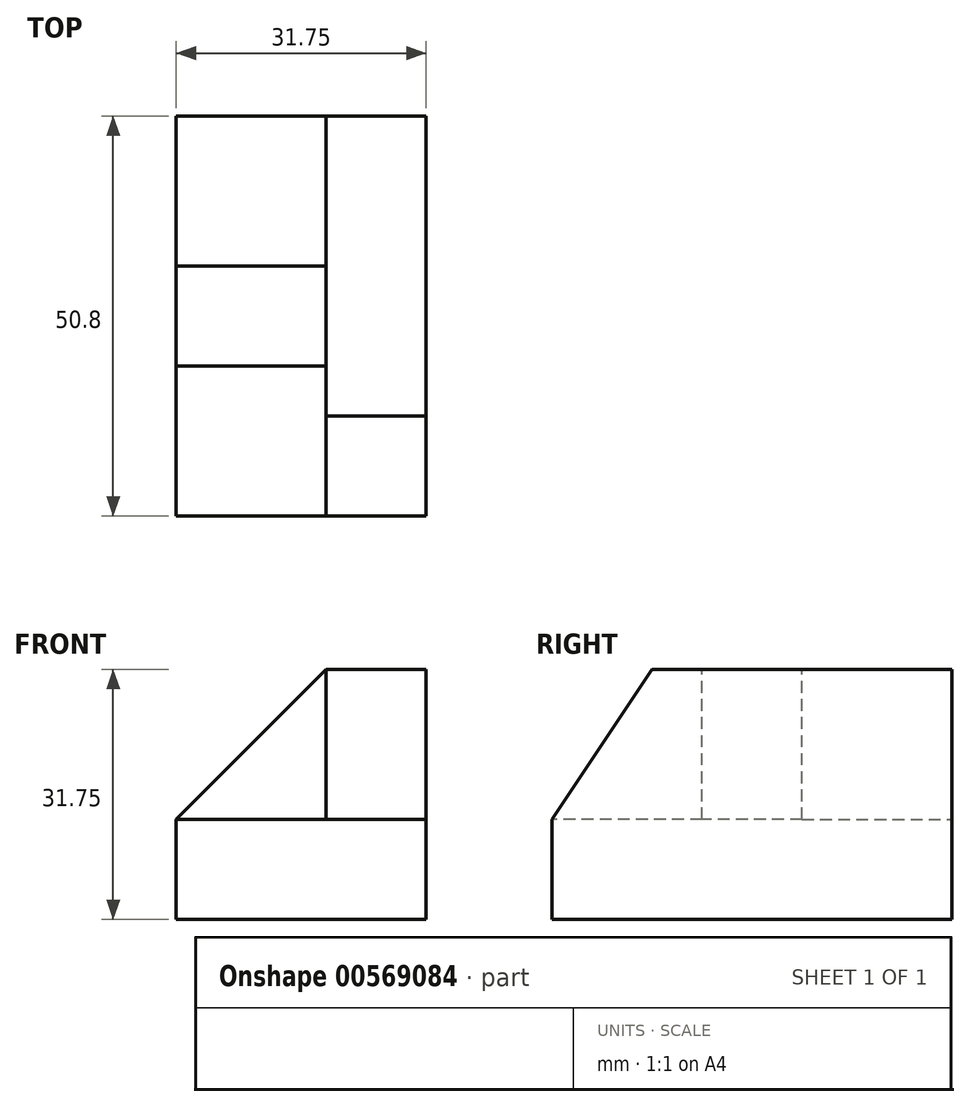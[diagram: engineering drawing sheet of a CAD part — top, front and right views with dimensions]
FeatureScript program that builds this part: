
annotation { "Feature Type Name" : "Feature", "Feature Type Description" : "" }
export const myFeature = defineFeature(function(context is Context, id is Id, definition is map)
    precondition{}
    {
        {
            var Q0;
            Q0=qCreatedBy(makeId("Top.planeOp"),FACE);
            var sketch = newSketch(context, id + "F0", { "sketchPlane" : qUnion([Q0])});
            skLineSegment(sketch, "E0", {"start": v(0, 0) * mm, "end": v(0, 50.8) * mm});
            skLineSegment(sketch, "E1", {"start": v(0, 50.8) * mm, "end": v(31.75, 50.8) * mm});
            skLineSegment(sketch, "E2", {"start": v(31.75, 50.8) * mm, "end": v(31.75, 0) * mm});
            skLineSegment(sketch, "E3", {"start": v(31.75, 0) * mm, "end": v(0, 0) * mm});
            skSolve(sketch);
        }
        {
            var Q0;
            Q0=makeQuery(id+"F0.imprint","IMPRINT",FACE,{"disambiguationData":[TD([[makeQuery(id+"F0.imprint","IMPRINT",EDGE,{"derivedFrom":sQuery(id+"F0.wireOp",EDGE,"E0")}),-1.0]])]});
            extrude(context, id + "F1", {"entities" : qUnion([Q0]), "depth" : 31.75 * mm, "offsetDistance" : 25.4 * mm});
        }
        {
            var Q0;
            Q0=makeQuery(id+"F1.opExtrude","CAP_FACE",FACE,{"disambiguationData":[OSD([sQuery(id+"F0.wireOp",EDGE,"E0"),sQuery(id+"F0.wireOp",EDGE,"E1"),sQuery(id+"F0.wireOp",EDGE,"E2"),sQuery(id+"F0.wireOp",EDGE,"E3")])],"isStart":false});
            var sketch = newSketch(context, id + "F2", { "sketchPlane" : qUnion([Q0])});
            skLineSegment(sketch, "E4", {"start": v(0, 19.05) * mm, "end": v(19.05, 19.05) * mm});
            skLineSegment(sketch, "E5", {"start": v(19.05, 19.05) * mm, "end": v(19.05, 0) * mm});
            skLineSegment(sketch, "E6", {"start": v(19.05, 0) * mm, "end": v(0, 0) * mm});
            skLineSegment(sketch, "E7", {"start": v(0, 0) * mm, "end": v(0, 19.05) * mm});
            skLineSegment(sketch, "E8", {"start": v(0, 31.75) * mm, "end": v(19.05, 31.75) * mm});
            skLineSegment(sketch, "E9", {"start": v(19.05, 31.75) * mm, "end": v(19.05, 50.8) * mm});
            skLineSegment(sketch, "E10", {"start": v(19.05, 50.8) * mm, "end": v(0, 50.8) * mm});
            skLineSegment(sketch, "E11", {"start": v(0, 50.8) * mm, "end": v(0, 31.75) * mm});
            skSolve(sketch);
        }
        {
            var Q0;
            Q0=makeQuery(id+"F2.imprint","IMPRINT",FACE,{"disambiguationData":[TD([[makeQuery(id+"F2.imprint","IMPRINT",EDGE,{"derivedFrom":sQuery(id+"F2.wireOp",EDGE,"E8")}),1.0]])]});
            var Q1;
            Q1=makeQuery(id+"F2.imprint","IMPRINT",FACE,{"disambiguationData":[TD([[makeQuery(id+"F2.imprint","IMPRINT",EDGE,{"derivedFrom":sQuery(id+"F2.wireOp",EDGE,"E4")}),-1.0]])]});
            extrude(context, id + "F3", {"entities" : qUnion([Q0, Q1]), "operationType" : NewBodyOperationType.REMOVE, "oppositeDirection" : true, "depth" : 19.05 * mm, "offsetDistance" : 25.4 * mm});
        }
        {
            var Q0;
            Q0=makeQuery(id+"F3.boolean.opBoolean","COPY",FACE,{"derivedFrom":makeQuery(id+"F3.opExtrude","SWEPT_FACE",FACE,{"disambiguationData":[OSD([sQuery(id+"F2.wireOp",EDGE,"E4")])]})});
            var sketch = newSketch(context, id + "F4", { "sketchPlane" : qUnion([Q0])});
            skLineSegment(sketch, "E12", {"start": v(0, 12.7) * mm, "end": v(19.05, 31.75) * mm});
            skLineSegment(sketch, "E13", {"start": v(19.05, 31.75) * mm, "end": v(0, 31.75) * mm});
            skLineSegment(sketch, "E14", {"start": v(0, 31.75) * mm, "end": v(0, 12.7) * mm});
            skSolve(sketch);
        }
        {
            var Q0;
            Q0=makeQuery(id+"F4.imprint","IMPRINT",FACE,{"disambiguationData":[TD([[makeQuery(id+"F4.imprint","IMPRINT",EDGE,{"derivedFrom":sQuery(id+"F4.wireOp",EDGE,"E12")}),1.0]])]});
            extrude(context, id + "F5", {"entities" : qUnion([Q0]), "operationType" : NewBodyOperationType.REMOVE, "oppositeDirection" : true, "depth" : 25.4 * mm, "offsetDistance" : 25.4 * mm});
        }
        {
            var Q0;
            Q0=makeQuery(id+"F3.boolean.opBoolean","COPY",FACE,{"derivedFrom":makeQuery(id+"F3.opExtrude","SWEPT_FACE",FACE,{"disambiguationData":[OSD([sQuery(id+"F2.wireOp",EDGE,"E5")])]})});
            var sketch = newSketch(context, id + "F6", { "sketchPlane" : qUnion([Q0])});
            skLineSegment(sketch, "E15", {"start": v(0, 31.75) * mm, "end": v(0, 12.7) * mm});
            skLineSegment(sketch, "E16", {"start": v(0, 12.7) * mm, "end": v(-12.7, 31.75) * mm});
            skLineSegment(sketch, "E17", {"start": v(-12.7, 31.75) * mm, "end": v(0, 31.75) * mm});
            skSolve(sketch);
        }
        {
            var Q0;
            Q0=makeQuery(id+"F6.imprint","IMPRINT",FACE,{"disambiguationData":[TD([[makeQuery(id+"F6.imprint","IMPRINT",EDGE,{"derivedFrom":sQuery(id+"F6.wireOp",EDGE,"E15")}),1.0]])]});
            extrude(context, id + "F7", {"entities" : qUnion([Q0]), "operationType" : NewBodyOperationType.REMOVE, "oppositeDirection" : true, "depth" : 25.4 * mm, "offsetDistance" : 25.4 * mm});
        }
    });
